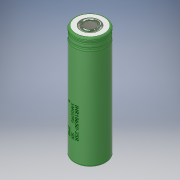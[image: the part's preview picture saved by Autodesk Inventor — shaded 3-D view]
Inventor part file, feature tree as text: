
AUTODESK INVENTOR PART (.ipt)
format: ipt  version: 2019.4 (Build 234330000, 330)  size: 1,021,952 bytes
history: native  units: mm
features: fillet x3, sketch x3, revolve x2, plane x1, emboss x1, chamfer x1
ambient origin geometry x8: Origin, YZ Plane, XZ Plane, XY Plane, X Axis, Y Axis, Z Axis, Center Point
bodies: Solid1 (feature_tree)
feature tree (11):
  revolve  "Revolution1"  [1 undecoded]
  fillet  "Fillet1"  [1 undecoded]
  plane  "Work Plane1"
  emboss  "Emboss2"
  revolve  "Revolution2"  [1 undecoded]
  chamfer  "Chamfer1"  Distance=20.0mm
  fillet  "Fillet4"  Radius=0.01mm
  fillet  "Fillet5"  Radius=3.5mm
  sketch  "Sketch1"  dims[d0=65.0mm d1=9.165mm d2=90.0deg]
  sketch  "Sketch4"  dims[d3=1.0mm d18=0.5mm]
  sketch  "Sketch6"  dims[d19=7.0mm d20=20.0mm d21=0.01mm d22=0.174533mm d23=3.5mm d27=0.7mm d28=2.5mm d29=0.0mm d30=6.0mm d31=90.0deg d32=0.4mm d33=0.4mm d34=0.5mm d35=45.0deg d36=1.0mm d37=2.0mm d38=2.0mm d39=10.0mm d40=0.0mm]
note: 3 required parameter values undecoded (feature->parameter linkage not recoverable at this tier; creation-order binding heuristic only, values carry confidence <= 0.55)